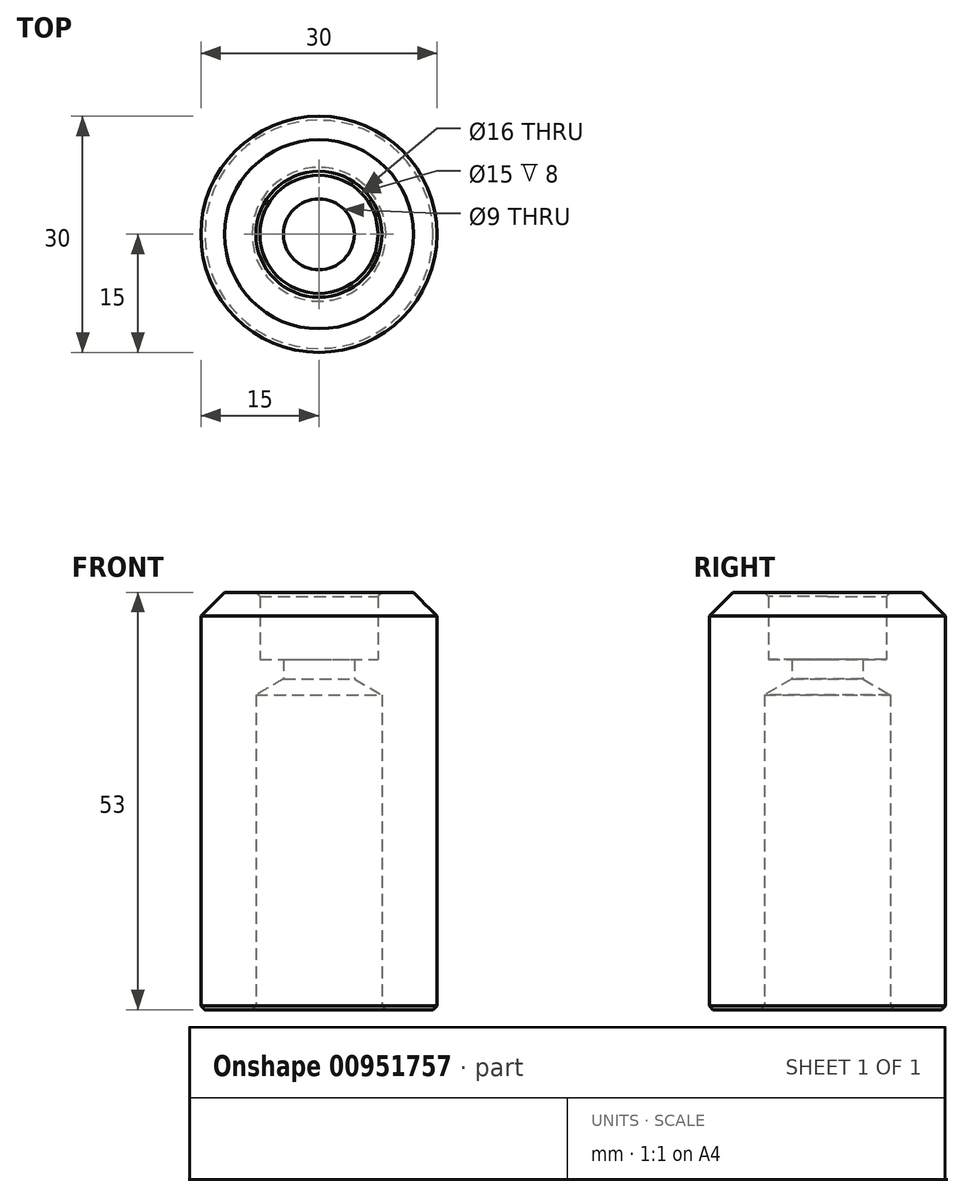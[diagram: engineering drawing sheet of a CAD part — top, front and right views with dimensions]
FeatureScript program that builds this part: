
annotation { "Feature Type Name" : "Feature", "Feature Type Description" : "" }
export const myFeature = defineFeature(function(context is Context, id is Id, definition is map)
    precondition{}
    {
        {
            var Q0;
            Q0=qCreatedBy(makeId("Front.planeOp"),FACE);
            var sketch = newSketch(context, id + "F0", { "sketchPlane" : qUnion([Q0])});
            skLineSegment(sketch, "E0", {"start": v(0, 0) * mm, "end": v(0, 66.29) * mm, "construction": true});
            skLineSegment(sketch, "E1", {"start": v(8, 0) * mm, "end": v(15, 0) * mm});
            skLineSegment(sketch, "E2", {"start": v(15, 0) * mm, "end": v(15, 53) * mm});
            skLineSegment(sketch, "E3", {"start": v(4.5, 42.02) * mm, "end": v(8, 40) * mm});
            skLineSegment(sketch, "E4", {"start": v(8, 40) * mm, "end": v(8, 0) * mm});
            skPoint(sketch, "E5.endSnap0", {"position": v(9.75, 47.71) * mm});
            skPoint(sketch, "E6.orphan", {"position": v(4.5, 42.43) * mm});
            skPoint(sketch, "E5.end.orphan", {"position": v(9.75, 42.22) * mm});
            skPoint(sketch, "E7.start.orphan", {"position": v(4.5, 42.22) * mm});
            skLineSegment(sketch, "E8", {"start": v(15, 53) * mm, "end": v(7.5, 53) * mm});
            skLineSegment(sketch, "E9", {"start": v(7.5, 53) * mm, "end": v(7.5, 44.5) * mm});
            skLineSegment(sketch, "E10", {"start": v(7.5, 44.5) * mm, "end": v(4.5, 44.5) * mm});
            skLineSegment(sketch, "E11", {"start": v(4.5, 44.5) * mm, "end": v(4.5, 42.02) * mm});
            skSolve(sketch);
        }
        {
            var Q0;
            Q0=makeQuery(id+"F0.imprint","IMPRINT",FACE,{"disambiguationData":[TD([[makeQuery(id+"F0.imprint","IMPRINT",EDGE,{"derivedFrom":sQuery(id+"F0.wireOp",EDGE,"E1")}),1.0]])]});
            var Q1;
            Q1=sQuery(id+"F0.wireOp",EDGE,"E0");
            revolve(context, id + "F1", {"surfaceOperationType" : NewSurfaceOperationType.NEW, "entities" : qUnion([Q0]), "axis" : qUnion([Q1]), "revolveType" : RevolveType.FULL});
        }
        {
            var Q0;
            Q0=makeQuery(id+"F1.opRevolve","SWEPT_EDGE",EDGE,{"disambiguationData":[OSD([sQuery(id+"F0.wireOp",EDGE,"E2"),sQuery(id+"F0.wireOp",EDGE,"E8")])]});
            chamfer(context, id + "F2", {"entities" : qUnion([Q0]), "width" : 3 * mm, "tangentPropagation" : true});
        }
        {
            var Q0;
            Q0=makeQuery(id+"F1.opRevolve","SWEPT_EDGE",EDGE,{"disambiguationData":[OSD([sQuery(id+"F0.wireOp",EDGE,"E8"),sQuery(id+"F0.wireOp",EDGE,"E9")])]});
            var Q1;
            Q1=makeQuery(id+"F1.opRevolve","SWEPT_EDGE",EDGE,{"disambiguationData":[OSD([sQuery(id+"F0.wireOp",EDGE,"E1"),sQuery(id+"F0.wireOp",EDGE,"E2")])]});
            var Q2;
            Q2=makeQuery(id+"F1.opRevolve","SWEPT_EDGE",EDGE,{"disambiguationData":[OSD([sQuery(id+"F0.wireOp",EDGE,"E1"),sQuery(id+"F0.wireOp",EDGE,"E4")])]});
            chamfer(context, id + "F3", {"entities" : qUnion([Q0, Q1, Q2]), "width" : 0.5 * mm, "tangentPropagation" : true});
        }
    });
